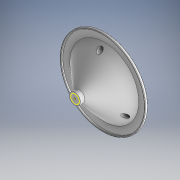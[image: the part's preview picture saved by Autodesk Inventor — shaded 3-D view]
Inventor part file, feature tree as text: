
AUTODESK INVENTOR PART (.ipt)
format: ipt  version: 2017.3 (Build 213256000, 256)  size: 437,248 bytes
history: native  units: mm
features: extrude x8, sketch x8, fillet x3, hole x3, draft x2, projected_geometry x2
ambient origin geometry x8: Origin, YZ Plane, XZ Plane, XY Plane, X Axis, Y Axis, Z Axis, Center Point
bodies: Solid1 (feature_tree)
feature tree (26):
  extrude  "Extrusion1"  Depth=82.0mm
  extrude  "Extrusion2"  Depth=10.0mm
  draft  "FaceDraft1"
  draft  "FaceDraft2"
  extrude  "Extrusion3"  Depth=8.552113mm
  extrude  "Extrusion4"  Depth=5.0mm TaperAngle=0.0deg
  extrude  "Extrusion6"  Depth=1.0mm TaperAngle=0.0deg
  fillet  "Fillet1"  Radius=1.5mm
  fillet  "Fillet2"  Radius=3.0mm
  fillet  "Fillet3"  Radius=0.5mm
  extrude  "Extrusion7"  Depth=2.0mm
  sketch  "Sketch11"  dims[d24=0.5mm d25=2.0mm]
  extrude  "Extrusion8"  Depth=1.0mm
  hole  "Hole1"  [1 undecoded]
  hole  "Hole2"  [1 undecoded]
  extrude  "Extrusion9"  Depth=10.0mm
  hole  "Hole3"  [1 undecoded]
  sketch  "Sketch4"  dims[d0=96.0mm d2=82.0mm]
  sketch  "Sketch5"  dims[d3=30.0mm d4=0.0mm d6=10.0mm]
  sketch  "Sketch6"  dims[d7=30.0mm d8=0.0mm d9=8.552113mm]
  sketch  "Sketch9"  dims[d10=8.552113mm d11=5.0mm d12=0.0mm]
  sketch  "Sketch10"  dims[d13=96.0mm d14=1.0mm d15=0.0mm d20=1.5mm d21=3.0mm d22=0.0mm d23=0.5mm]
  sketch  "Sketch12"  dims[d42=1.0mm d43=0.0mm d45=20.0mm]
  sketch  "Sketch13"  dims[d46=20.0mm d47=20.0mm d48=20.0mm d49=2.0mm d50=2.0mm d51=2.0mm d52=2.0mm d53=15.0mm d54=7.0mm d55=6.0mm d56=6.0mm d57=6.0mm d58=82.0mm d60=7.0mm d61=6.0mm d62=6.0mm d63=6.0mm d64=2.0mm d65=2.0mm d66=2.0mm d67=10.0mm d68=0.0mm d69=6.0mm d70=6.0mm d71=4.0mm d72=2.0mm d73=90.0deg d74=8.0mm d75=20.594885mm d76=6.0mm d77=6.0mm d78=4.0mm d79=2.0mm d80=90.0deg d81=8.0mm d82=20.594885mm d83=5.0mm d84=0.0mm d85=2.0mm d86=5.984mm d87=10.0mm d88=2.0mm d89=90.0deg d90=8.0mm d91=20.594885mm]
  projected_geometry  "Projected Loop1"
  projected_geometry  "Projected Loop2"
note: 3 required parameter values undecoded (feature->parameter linkage not recoverable at this tier; creation-order binding heuristic only, values carry confidence <= 0.55)
